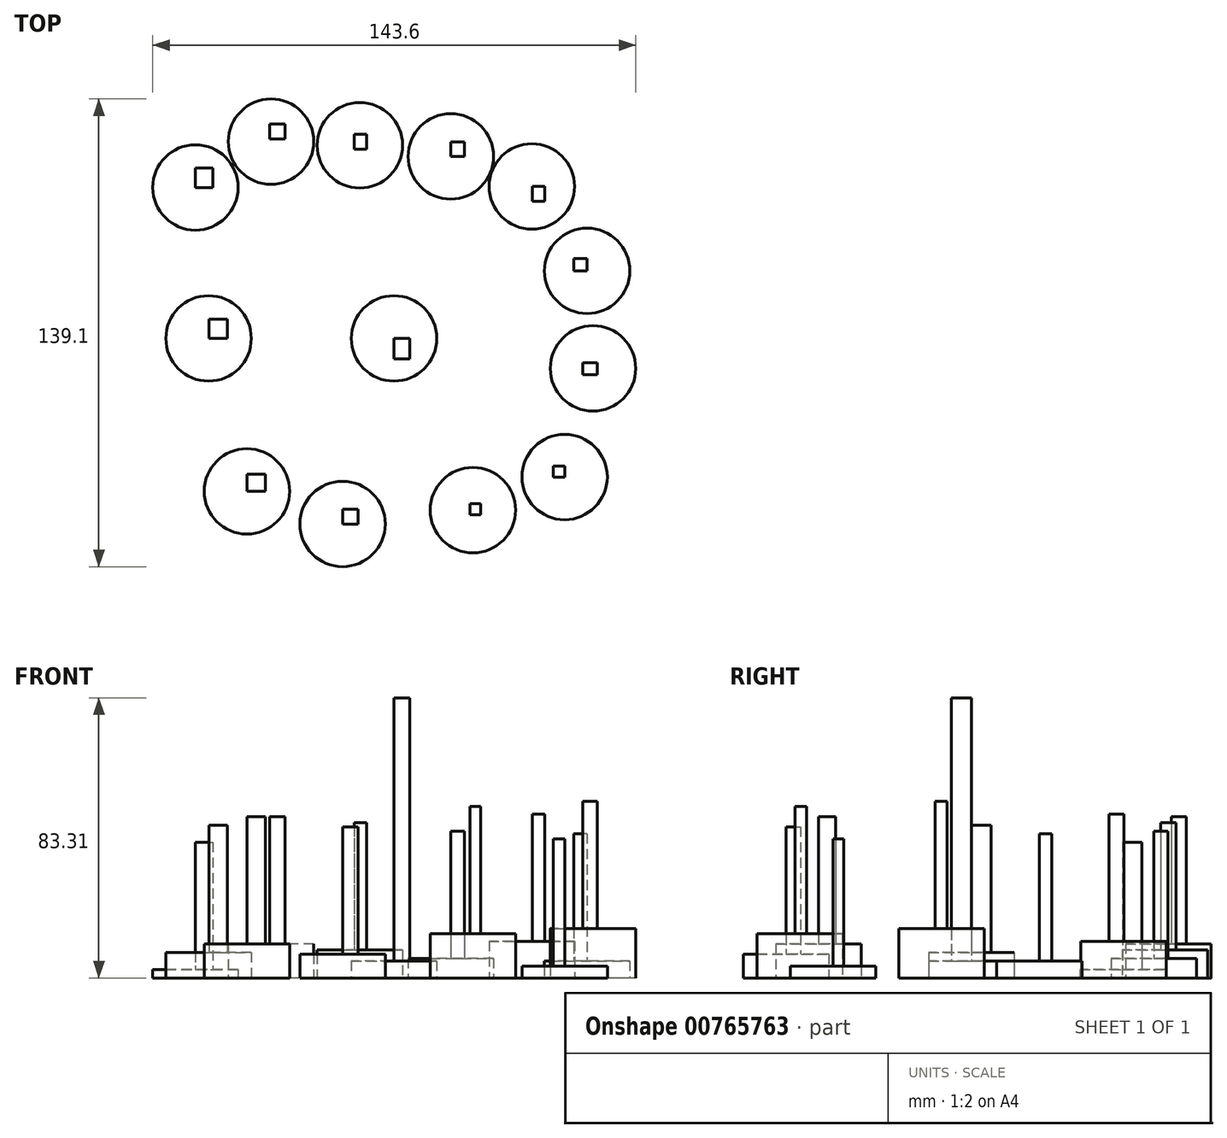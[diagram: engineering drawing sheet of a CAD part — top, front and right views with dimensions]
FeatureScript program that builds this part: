
annotation { "Feature Type Name" : "Feature", "Feature Type Description" : "" }
export const myFeature = defineFeature(function(context is Context, id is Id, definition is map)
    precondition{}
    {
        {
            var Q0;
            Q0=qCreatedBy(makeId("Top.planeOp"),FACE);
            var sketch = newSketch(context, id + "F0", { "sketchPlane" : qUnion([Q0])});
            skCircle(sketch, "E0", {"center": v(0, 0) * mm, "radius": 12.7 * mm});
            skSolve(sketch);
        }
        {
            var Q0;
            Q0=makeQuery(id+"F0.imprint","IMPRINT",FACE,{"disambiguationData":[TD([[makeQuery(id+"F0.imprint","IMPRINT",EDGE,{"derivedFrom":sQuery(id+"F0.wireOp",EDGE,"E0")}),1.0]])]});
            var sketch = newSketch(context, id + "F1", { "sketchPlane" : qUnion([Q0])});
            skSolve(sketch);
        }
        {
            var Q0;
            Q0 = qSketchRegion(id + "F1", true);
            var Q1;
            Q1=makeQuery(id+"F1.imprint","IMPRINT",FACE,{"disambiguationData":[TD([[makeQuery(id+"F1.imprint","IMPRINT",EDGE,{"derivedFrom":makeQuery(id+"F0.imprint","IMPRINT",EDGE,{"derivedFrom":sQuery(id+"F0.wireOp",EDGE,"E0")})}),1.0]])]});
            extrude(context, id + "F2", {"entities" : qUnion([Q0, Q1]), "depth" : 5.08 * mm, "offsetDistance" : 25.4 * mm});
        }
        {
            var Q0;
            Q0=qCreatedBy(makeId("Top.planeOp"),FACE);
            var sketch = newSketch(context, id + "F3", { "sketchPlane" : qUnion([Q0])});
            skCircle(sketch, "E1", {"center": v(-55.13, 0) * mm, "radius": 12.7 * mm});
            skSolve(sketch);
        }
        {
            var Q0;
            Q0=makeQuery(id+"F3.imprint","IMPRINT",FACE,{"disambiguationData":[TD([[makeQuery(id+"F3.imprint","IMPRINT",EDGE,{"derivedFrom":sQuery(id+"F3.wireOp",EDGE,"E1")}),1.0]])]});
            extrude(context, id + "F4", {"entities" : qUnion([Q0]), "depth" : 7.62 * mm, "offsetDistance" : 25.4 * mm});
        }
        {
            var Q0;
            Q0=qCreatedBy(makeId("Top.planeOp"),FACE);
            var sketch = newSketch(context, id + "F5", { "sketchPlane" : qUnion([Q0])});
            skCircle(sketch, "E2", {"center": v(-43.74, -45.49) * mm, "radius": 12.7 * mm});
            skSolve(sketch);
        }
        {
            var Q0;
            Q0=makeQuery(id+"F5.imprint","IMPRINT",FACE,{"disambiguationData":[TD([[makeQuery(id+"F5.imprint","IMPRINT",EDGE,{"derivedFrom":sQuery(id+"F5.wireOp",EDGE,"E2")}),1.0]])]});
            extrude(context, id + "F6", {"entities" : qUnion([Q0]), "depth" : 10.16 * mm, "offsetDistance" : 25.4 * mm});
        }
        {
            var Q0;
            Q0=qCreatedBy(makeId("Top.planeOp"),FACE);
            var sketch = newSketch(context, id + "F7", { "sketchPlane" : qUnion([Q0])});
            skCircle(sketch, "E3", {"center": v(-59.04, 44.9) * mm, "radius": 12.7 * mm});
            skSolve(sketch);
        }
        {
            var Q0;
            Q0=makeQuery(id+"F7.imprint","IMPRINT",FACE,{"disambiguationData":[TD([[makeQuery(id+"F7.imprint","IMPRINT",EDGE,{"derivedFrom":sQuery(id+"F7.wireOp",EDGE,"E3")}),1.0]])]});
            extrude(context, id + "F8", {"entities" : qUnion([Q0]), "depth" : 2.54 * mm, "offsetDistance" : 25.4 * mm});
        }
        {
            var Q0;
            Q0=qCreatedBy(makeId("Top.planeOp"),FACE);
            var sketch = newSketch(context, id + "F9", { "sketchPlane" : qUnion([Q0])});
            skCircle(sketch, "E4", {"center": v(-36.56, 58.52) * mm, "radius": 12.7 * mm});
            skSolve(sketch);
        }
        {
            var Q0;
            Q0 = qSketchRegion(id + "F9", true);
            extrude(context, id + "F10", {"entities" : qUnion([Q0]), "depth" : 10.16 * mm, "offsetDistance" : 25.4 * mm});
        }
        {
            var Q0;
            Q0=qCreatedBy(makeId("Top.planeOp"),FACE);
            var sketch = newSketch(context, id + "F11", { "sketchPlane" : qUnion([Q0])});
            skCircle(sketch, "E5", {"center": v(-10.16, 57.45) * mm, "radius": 12.7 * mm});
            skSolve(sketch);
        }
        {
            var Q0;
            Q0 = qSketchRegion(id + "F11", true);
            extrude(context, id + "F12", {"entities" : qUnion([Q0]), "depth" : 8.38 * mm, "offsetDistance" : 25.4 * mm});
        }
        {
            var Q0;
            Q0=qCreatedBy(makeId("Top.planeOp"),FACE);
            var sketch = newSketch(context, id + "F13", { "sketchPlane" : qUnion([Q0])});
            skCircle(sketch, "E6", {"center": v(16.88, 54.13) * mm, "radius": 12.7 * mm});
            skSolve(sketch);
        }
        {
            var Q0;
            Q0=makeQuery(id+"F13.imprint","IMPRINT",FACE,{"disambiguationData":[TD([[makeQuery(id+"F13.imprint","IMPRINT",EDGE,{"derivedFrom":sQuery(id+"F13.wireOp",EDGE,"E6")}),1.0]])]});
            extrude(context, id + "F14", {"entities" : qUnion([Q0]), "depth" : 5.84 * mm, "offsetDistance" : 25.4 * mm});
        }
        {
            var Q0;
            Q0=qCreatedBy(makeId("Top.planeOp"),FACE);
            var sketch = newSketch(context, id + "F15", { "sketchPlane" : qUnion([Q0])});
            skCircle(sketch, "E7", {"center": v(40.97, 45.2) * mm, "radius": 12.7 * mm});
            skSolve(sketch);
        }
        {
            var Q0;
            Q0 = qSketchRegion(id + "F15", true);
            extrude(context, id + "F16", {"entities" : qUnion([Q0]), "depth" : 10.92 * mm, "offsetDistance" : 25.4 * mm});
        }
        {
            var Q0;
            Q0=qCreatedBy(makeId("Top.planeOp"),FACE);
            var sketch = newSketch(context, id + "F17", { "sketchPlane" : qUnion([Q0])});
            skCircle(sketch, "E8", {"center": v(57.42, 20.1) * mm, "radius": 12.7 * mm});
            skSolve(sketch);
        }
        {
            var Q0;
            Q0 = qSketchRegion(id + "F17", true);
            extrude(context, id + "F18", {"entities" : qUnion([Q0]), "depth" : 5.08 * mm, "offsetDistance" : 25.4 * mm});
        }
        {
            var Q0;
            Q0=qCreatedBy(makeId("Top.planeOp"),FACE);
            var sketch = newSketch(context, id + "F19", { "sketchPlane" : qUnion([Q0])});
            skCircle(sketch, "E9", {"center": v(59.16, -8.92) * mm, "radius": 12.7 * mm});
            skSolve(sketch);
        }
        {
            var Q0;
            Q0 = qSketchRegion(id + "F19", true);
            var Q1;
            Q1=makeQuery(id+"F19.imprint","IMPRINT",FACE,{"disambiguationData":[TD([[makeQuery(id+"F19.imprint","IMPRINT",EDGE,{"derivedFrom":sQuery(id+"F19.wireOp",EDGE,"E9")}),1.0]])]});
            extrude(context, id + "F20", {"entities" : qUnion([Q0, Q1]), "depth" : 14.73 * mm, "offsetDistance" : 25.4 * mm});
        }
        {
            var Q0;
            Q0=qCreatedBy(makeId("Top.planeOp"),FACE);
            var sketch = newSketch(context, id + "F21", { "sketchPlane" : qUnion([Q0])});
            skCircle(sketch, "E10", {"center": v(50.72, -41.21) * mm, "radius": 12.7 * mm});
            skSolve(sketch);
        }
        {
            var Q0;
            Q0 = qSketchRegion(id + "F21", true);
            extrude(context, id + "F22", {"entities" : qUnion([Q0]), "depth" : 3.56 * mm, "offsetDistance" : 25.4 * mm});
        }
        {
            var Q0;
            Q0=qCreatedBy(makeId("Top.planeOp"),FACE);
            var sketch = newSketch(context, id + "F23", { "sketchPlane" : qUnion([Q0])});
            skCircle(sketch, "E11", {"center": v(23.45, -51.08) * mm, "radius": 12.7 * mm});
            skSolve(sketch);
        }
        {
            var Q0;
            Q0 = qSketchRegion(id + "F23", true);
            extrude(context, id + "F24", {"entities" : qUnion([Q0]), "depth" : 13.2 * mm, "offsetDistance" : 25.4 * mm});
        }
        {
            var Q0;
            Q0=qCreatedBy(makeId("Top.planeOp"),FACE);
            var sketch = newSketch(context, id + "F25", { "sketchPlane" : qUnion([Q0])});
            skCircle(sketch, "E12", {"center": v(-15.3, -55.18) * mm, "radius": 12.7 * mm});
            skSolve(sketch);
        }
        {
            var Q0;
            Q0=makeQuery(id+"F25.imprint","IMPRINT",FACE,{"disambiguationData":[TD([[makeQuery(id+"F25.imprint","IMPRINT",EDGE,{"derivedFrom":sQuery(id+"F25.wireOp",EDGE,"E12")}),1.0]])]});
            extrude(context, id + "F26", {"entities" : qUnion([Q0]), "depth" : 7.11 * mm, "offsetDistance" : 25.4 * mm});
        }
        {
            var Q0;
            Q0=makeQuery(id+"F2.opExtrude","CAP_FACE",FACE,{"disambiguationData":[OSD([sQuery(id+"F0.wireOp",EDGE,"E0")])],"isStart":false});
            var sketch = newSketch(context, id + "F27", { "sketchPlane" : qUnion([Q0])});
            skSolve(sketch);
        }
        {
            var Q0;
            Q0=makeQuery(id+"F27.imprint","IMPRINT",FACE,{"disambiguationData":[TD([[makeQuery(id+"F27.imprint","IMPRINT",EDGE,{"derivedFrom":makeQuery(id+"F2.opExtrude","CAP_EDGE",EDGE,{"disambiguationData":[OSD([sQuery(id+"F0.wireOp",EDGE,"E0")])],"isStart":false})}),1.0]])]});
            var sketch = newSketch(context, id + "F28", { "sketchPlane" : qUnion([Q0])});
            skLineSegment(sketch, "E13.bottom", {"start": v(0, -6.04) * mm, "end": v(4.65, -6.04) * mm});
            skLineSegment(sketch, "E13.top", {"start": v(0, 0) * mm, "end": v(4.65, 0) * mm});
            skLineSegment(sketch, "E13.left", {"start": v(0, -6.04) * mm, "end": v(0, 0) * mm});
            skLineSegment(sketch, "E13.right", {"start": v(4.65, -6.04) * mm, "end": v(4.65, 0) * mm});
            skSolve(sketch);
        }
        {
            var Q0;
            Q0 = qSketchRegion(id + "F28", true);
            extrude(context, id + "F29", {"entities" : qUnion([Q0]), "operationType" : NewBodyOperationType.ADD, "depth" : 78.23 * mm, "offsetDistance" : 25.4 * mm});
        }
        {
            var Q0;
            Q0=makeQuery(id+"F6.opExtrude","CAP_FACE",FACE,{"disambiguationData":[OSD([sQuery(id+"F5.wireOp",EDGE,"E2")])],"isStart":false});
            var sketch = newSketch(context, id + "F30", { "sketchPlane" : qUnion([Q0])});
            skLineSegment(sketch, "E14.bottom", {"start": v(-43.74, -45.49) * mm, "end": v(-38.19, -45.49) * mm});
            skLineSegment(sketch, "E14.top", {"start": v(-43.74, -40.41) * mm, "end": v(-38.19, -40.41) * mm});
            skLineSegment(sketch, "E14.left", {"start": v(-43.74, -45.49) * mm, "end": v(-43.74, -40.41) * mm});
            skLineSegment(sketch, "E14.right", {"start": v(-38.19, -45.49) * mm, "end": v(-38.19, -40.41) * mm});
            skSolve(sketch);
        }
        {
            var Q0;
            Q0 = qSketchRegion(id + "F30", true);
            extrude(context, id + "F31", {"entities" : qUnion([Q0]), "operationType" : NewBodyOperationType.ADD, "depth" : 37.85 * mm, "offsetDistance" : 25.4 * mm});
        }
        {
            var Q0;
            Q0=makeQuery(id+"F4.opExtrude","CAP_FACE",FACE,{"disambiguationData":[OSD([sQuery(id+"F3.wireOp",EDGE,"E1")])],"isStart":false});
            var sketch = newSketch(context, id + "F32", { "sketchPlane" : qUnion([Q0])});
            skSolve(sketch);
        }
        {
            var Q0;
            Q0=makeQuery(id+"F32.imprint","IMPRINT",FACE,{"disambiguationData":[TD([[makeQuery(id+"F32.imprint","IMPRINT",EDGE,{"derivedFrom":makeQuery(id+"F4.opExtrude","CAP_EDGE",EDGE,{"disambiguationData":[OSD([sQuery(id+"F3.wireOp",EDGE,"E1")])],"isStart":false})}),1.0]])]});
            var sketch = newSketch(context, id + "F33", { "sketchPlane" : qUnion([Q0])});
            skLineSegment(sketch, "E15.bottom", {"start": v(-55, 0) * mm, "end": v(-49.52, 0) * mm});
            skLineSegment(sketch, "E15.top", {"start": v(-55, 5.78) * mm, "end": v(-49.52, 5.78) * mm});
            skLineSegment(sketch, "E15.left", {"start": v(-55, 0) * mm, "end": v(-55, 5.78) * mm});
            skLineSegment(sketch, "E15.right", {"start": v(-49.52, 0) * mm, "end": v(-49.52, 5.78) * mm});
            skSolve(sketch);
        }
        {
            var Q0;
            Q0 = qSketchRegion(id + "F33", true);
            extrude(context, id + "F34", {"entities" : qUnion([Q0]), "operationType" : NewBodyOperationType.ADD, "depth" : 37.85 * mm, "offsetDistance" : 25.4 * mm});
        }
        {
            var Q0;
            Q0=makeQuery(id+"F8.opExtrude","CAP_FACE",FACE,{"disambiguationData":[OSD([sQuery(id+"F7.wireOp",EDGE,"E3")])],"isStart":false});
            var sketch = newSketch(context, id + "F35", { "sketchPlane" : qUnion([Q0])});
            skLineSegment(sketch, "E16.bottom", {"start": v(-59.04, 44.9) * mm, "end": v(-53.87, 44.9) * mm});
            skLineSegment(sketch, "E16.top", {"start": v(-59.04, 50.63) * mm, "end": v(-53.87, 50.63) * mm});
            skLineSegment(sketch, "E16.left", {"start": v(-59.04, 44.9) * mm, "end": v(-59.04, 50.63) * mm});
            skLineSegment(sketch, "E16.right", {"start": v(-53.87, 44.9) * mm, "end": v(-53.87, 50.63) * mm});
            skSolve(sketch);
        }
        {
            var Q0;
            Q0 = qSketchRegion(id + "F35", true);
            extrude(context, id + "F36", {"entities" : qUnion([Q0]), "operationType" : NewBodyOperationType.ADD, "depth" : 37.85 * mm, "offsetDistance" : 25.4 * mm});
        }
        {
            var Q0;
            Q0=makeQuery(id+"F10.opExtrude","CAP_FACE",FACE,{"disambiguationData":[OSD([sQuery(id+"F9.wireOp",EDGE,"E4")])],"isStart":false});
            var sketch = newSketch(context, id + "F37", { "sketchPlane" : qUnion([Q0])});
            skLineSegment(sketch, "E17.bottom", {"start": v(-32.45, 59.36) * mm, "end": v(-36.97, 59.36) * mm});
            skLineSegment(sketch, "E17.top", {"start": v(-32.45, 63.81) * mm, "end": v(-36.97, 63.81) * mm});
            skLineSegment(sketch, "E17.left", {"start": v(-32.45, 59.36) * mm, "end": v(-32.45, 63.81) * mm});
            skLineSegment(sketch, "E17.right", {"start": v(-36.97, 59.36) * mm, "end": v(-36.97, 63.81) * mm});
            skSolve(sketch);
        }
        {
            var Q0;
            Q0 = qSketchRegion(id + "F37", true);
            extrude(context, id + "F38", {"entities" : qUnion([Q0]), "operationType" : NewBodyOperationType.ADD, "depth" : 37.85 * mm, "offsetDistance" : 25.4 * mm});
        }
        {
            var Q0;
            Q0=makeQuery(id+"F12.opExtrude","CAP_FACE",FACE,{"disambiguationData":[OSD([sQuery(id+"F11.wireOp",EDGE,"E5")])],"isStart":false});
            var sketch = newSketch(context, id + "F39", { "sketchPlane" : qUnion([Q0])});
            skLineSegment(sketch, "E18.bottom", {"start": v(-11.8, 56.26) * mm, "end": v(-8.1, 56.26) * mm});
            skLineSegment(sketch, "E18.top", {"start": v(-11.8, 60.72) * mm, "end": v(-8.1, 60.72) * mm});
            skLineSegment(sketch, "E18.left", {"start": v(-11.8, 56.26) * mm, "end": v(-11.8, 60.72) * mm});
            skLineSegment(sketch, "E18.right", {"start": v(-8.1, 56.26) * mm, "end": v(-8.1, 60.72) * mm});
            skSolve(sketch);
        }
        {
            var Q0;
            Q0 = qSketchRegion(id + "F39", true);
            extrude(context, id + "F40", {"entities" : qUnion([Q0]), "operationType" : NewBodyOperationType.ADD, "depth" : 37.85 * mm, "offsetDistance" : 25.4 * mm});
        }
        {
            var Q0;
            Q0=makeQuery(id+"F14.opExtrude","CAP_FACE",FACE,{"disambiguationData":[OSD([sQuery(id+"F13.wireOp",EDGE,"E6")])],"isStart":false});
            var sketch = newSketch(context, id + "F41", { "sketchPlane" : qUnion([Q0])});
            skLineSegment(sketch, "E19.bottom", {"start": v(16.88, 54.13) * mm, "end": v(20.95, 54.13) * mm});
            skLineSegment(sketch, "E19.top", {"start": v(16.88, 58.37) * mm, "end": v(20.95, 58.37) * mm});
            skLineSegment(sketch, "E19.left", {"start": v(16.88, 54.13) * mm, "end": v(16.88, 58.37) * mm});
            skLineSegment(sketch, "E19.right", {"start": v(20.95, 54.13) * mm, "end": v(20.95, 58.37) * mm});
            skSolve(sketch);
        }
        {
            var Q0;
            Q0 = qSketchRegion(id + "F41", true);
            extrude(context, id + "F42", {"entities" : qUnion([Q0]), "operationType" : NewBodyOperationType.ADD, "depth" : 37.85 * mm, "offsetDistance" : 25.4 * mm});
        }
        {
            var Q0;
            Q0=makeQuery(id+"F16.opExtrude","CAP_FACE",FACE,{"disambiguationData":[OSD([sQuery(id+"F15.wireOp",EDGE,"E7")])],"isStart":false});
            var sketch = newSketch(context, id + "F43", { "sketchPlane" : qUnion([Q0])});
            skLineSegment(sketch, "E20.bottom", {"start": v(41.11, 40.78) * mm, "end": v(44.82, 40.78) * mm});
            skLineSegment(sketch, "E20.top", {"start": v(41.11, 45.24) * mm, "end": v(44.82, 45.24) * mm});
            skLineSegment(sketch, "E20.left", {"start": v(41.11, 40.78) * mm, "end": v(41.11, 45.24) * mm});
            skLineSegment(sketch, "E20.right", {"start": v(44.82, 40.78) * mm, "end": v(44.82, 45.24) * mm});
            skSolve(sketch);
        }
        {
            var Q0;
            Q0=makeQuery(id+"F43.imprint","IMPRINT",FACE,{"disambiguationData":[TD([[makeQuery(id+"F43.imprint","IMPRINT",EDGE,{"derivedFrom":sQuery(id+"F43.wireOp",EDGE,"E20.bottom")}),1.0]])]});
            extrude(context, id + "F44", {"entities" : qUnion([Q0]), "operationType" : NewBodyOperationType.ADD, "depth" : 37.85 * mm, "offsetDistance" : 25.4 * mm});
        }
        {
            var Q0;
            Q0=makeQuery(id+"F18.opExtrude","CAP_FACE",FACE,{"disambiguationData":[OSD([sQuery(id+"F17.wireOp",EDGE,"E8")])],"isStart":false});
            var sketch = newSketch(context, id + "F45", { "sketchPlane" : qUnion([Q0])});
            skLineSegment(sketch, "E21.bottom", {"start": v(57.42, 20.1) * mm, "end": v(53.5, 20.1) * mm});
            skLineSegment(sketch, "E21.top", {"start": v(57.42, 23.76) * mm, "end": v(53.5, 23.76) * mm});
            skLineSegment(sketch, "E21.left", {"start": v(57.42, 20.1) * mm, "end": v(57.42, 23.76) * mm});
            skLineSegment(sketch, "E21.right", {"start": v(53.5, 20.1) * mm, "end": v(53.5, 23.76) * mm});
            skSolve(sketch);
        }
        {
            var Q0;
            Q0 = qSketchRegion(id + "F45", true);
            extrude(context, id + "F46", {"entities" : qUnion([Q0]), "operationType" : NewBodyOperationType.ADD, "depth" : 37.85 * mm, "offsetDistance" : 25.4 * mm});
        }
        {
            var Q0;
            Q0=makeQuery(id+"F20.opExtrude","CAP_FACE",FACE,{"disambiguationData":[OSD([sQuery(id+"F19.wireOp",EDGE,"E9")])],"isStart":false});
            var sketch = newSketch(context, id + "F47", { "sketchPlane" : qUnion([Q0])});
            skLineSegment(sketch, "E22.bottom", {"start": v(60.48, -10.79) * mm, "end": v(56.1, -10.79) * mm});
            skLineSegment(sketch, "E22.top", {"start": v(60.48, -7.24) * mm, "end": v(56.1, -7.24) * mm});
            skLineSegment(sketch, "E22.left", {"start": v(60.48, -10.79) * mm, "end": v(60.48, -7.24) * mm});
            skLineSegment(sketch, "E22.right", {"start": v(56.1, -10.79) * mm, "end": v(56.1, -7.24) * mm});
            skSolve(sketch);
        }
        {
            var Q0;
            Q0 = qSketchRegion(id + "F47", true);
            var Q1;
            Q1=makeQuery(id+"F47.imprint","IMPRINT",FACE,{"disambiguationData":[TD([[makeQuery(id+"F47.imprint","IMPRINT",EDGE,{"derivedFrom":sQuery(id+"F47.wireOp",EDGE,"E22.bottom")}),-1.0]])]});
            extrude(context, id + "F48", {"entities" : qUnion([Q0, Q1]), "operationType" : NewBodyOperationType.ADD, "depth" : 37.85 * mm, "offsetDistance" : 25.4 * mm});
        }
        {
            var Q0;
            Q0=makeQuery(id+"F22.opExtrude","CAP_FACE",FACE,{"disambiguationData":[OSD([sQuery(id+"F21.wireOp",EDGE,"E10")])],"isStart":false});
            var sketch = newSketch(context, id + "F49", { "sketchPlane" : qUnion([Q0])});
            skLineSegment(sketch, "E23.bottom", {"start": v(50.72, -41.21) * mm, "end": v(47.31, -41.21) * mm});
            skLineSegment(sketch, "E23.top", {"start": v(50.72, -38.03) * mm, "end": v(47.31, -38.03) * mm});
            skLineSegment(sketch, "E23.left", {"start": v(50.72, -41.21) * mm, "end": v(50.72, -38.03) * mm});
            skLineSegment(sketch, "E23.right", {"start": v(47.31, -41.21) * mm, "end": v(47.31, -38.03) * mm});
            skSolve(sketch);
        }
        {
            var Q0;
            Q0 = qSketchRegion(id + "F49", true);
            extrude(context, id + "F50", {"entities" : qUnion([Q0]), "operationType" : NewBodyOperationType.ADD, "depth" : 37.85 * mm, "offsetDistance" : 25.4 * mm});
        }
        {
            var Q0;
            Q0=makeQuery(id+"F24.opExtrude","CAP_FACE",FACE,{"disambiguationData":[OSD([sQuery(id+"F23.wireOp",EDGE,"E11")])],"isStart":false});
            var sketch = newSketch(context, id + "F51", { "sketchPlane" : qUnion([Q0])});
            skLineSegment(sketch, "E24.bottom", {"start": v(22.63, -52.45) * mm, "end": v(25.8, -52.45) * mm});
            skLineSegment(sketch, "E24.top", {"start": v(22.63, -49.12) * mm, "end": v(25.8, -49.12) * mm});
            skLineSegment(sketch, "E24.left", {"start": v(22.63, -52.45) * mm, "end": v(22.63, -49.12) * mm});
            skLineSegment(sketch, "E24.right", {"start": v(25.8, -52.45) * mm, "end": v(25.8, -49.12) * mm});
            skSolve(sketch);
        }
        {
            var Q0;
            Q0=makeQuery(id+"F51.imprint","IMPRINT",FACE,{"disambiguationData":[TD([[makeQuery(id+"F51.imprint","IMPRINT",EDGE,{"derivedFrom":sQuery(id+"F51.wireOp",EDGE,"E24.bottom")}),1.0]])]});
            extrude(context, id + "F52", {"entities" : qUnion([Q0]), "operationType" : NewBodyOperationType.ADD, "depth" : 37.85 * mm, "offsetDistance" : 25.4 * mm});
        }
        {
            var Q0;
            Q0=makeQuery(id+"F26.opExtrude","CAP_FACE",FACE,{"disambiguationData":[OSD([sQuery(id+"F25.wireOp",EDGE,"E12")])],"isStart":false});
            var sketch = newSketch(context, id + "F53", { "sketchPlane" : qUnion([Q0])});
            skLineSegment(sketch, "E25.bottom", {"start": v(-15.3, -55.18) * mm, "end": v(-10.69, -55.18) * mm});
            skLineSegment(sketch, "E25.top", {"start": v(-15.3, -50.84) * mm, "end": v(-10.69, -50.84) * mm});
            skLineSegment(sketch, "E25.left", {"start": v(-15.3, -55.18) * mm, "end": v(-15.3, -50.84) * mm});
            skLineSegment(sketch, "E25.right", {"start": v(-10.69, -55.18) * mm, "end": v(-10.69, -50.84) * mm});
            skSolve(sketch);
        }
        {
            var Q0;
            Q0 = qSketchRegion(id + "F53", true);
            extrude(context, id + "F54", {"entities" : qUnion([Q0]), "operationType" : NewBodyOperationType.ADD, "depth" : 37.85 * mm, "offsetDistance" : 25.4 * mm});
        }
    });
